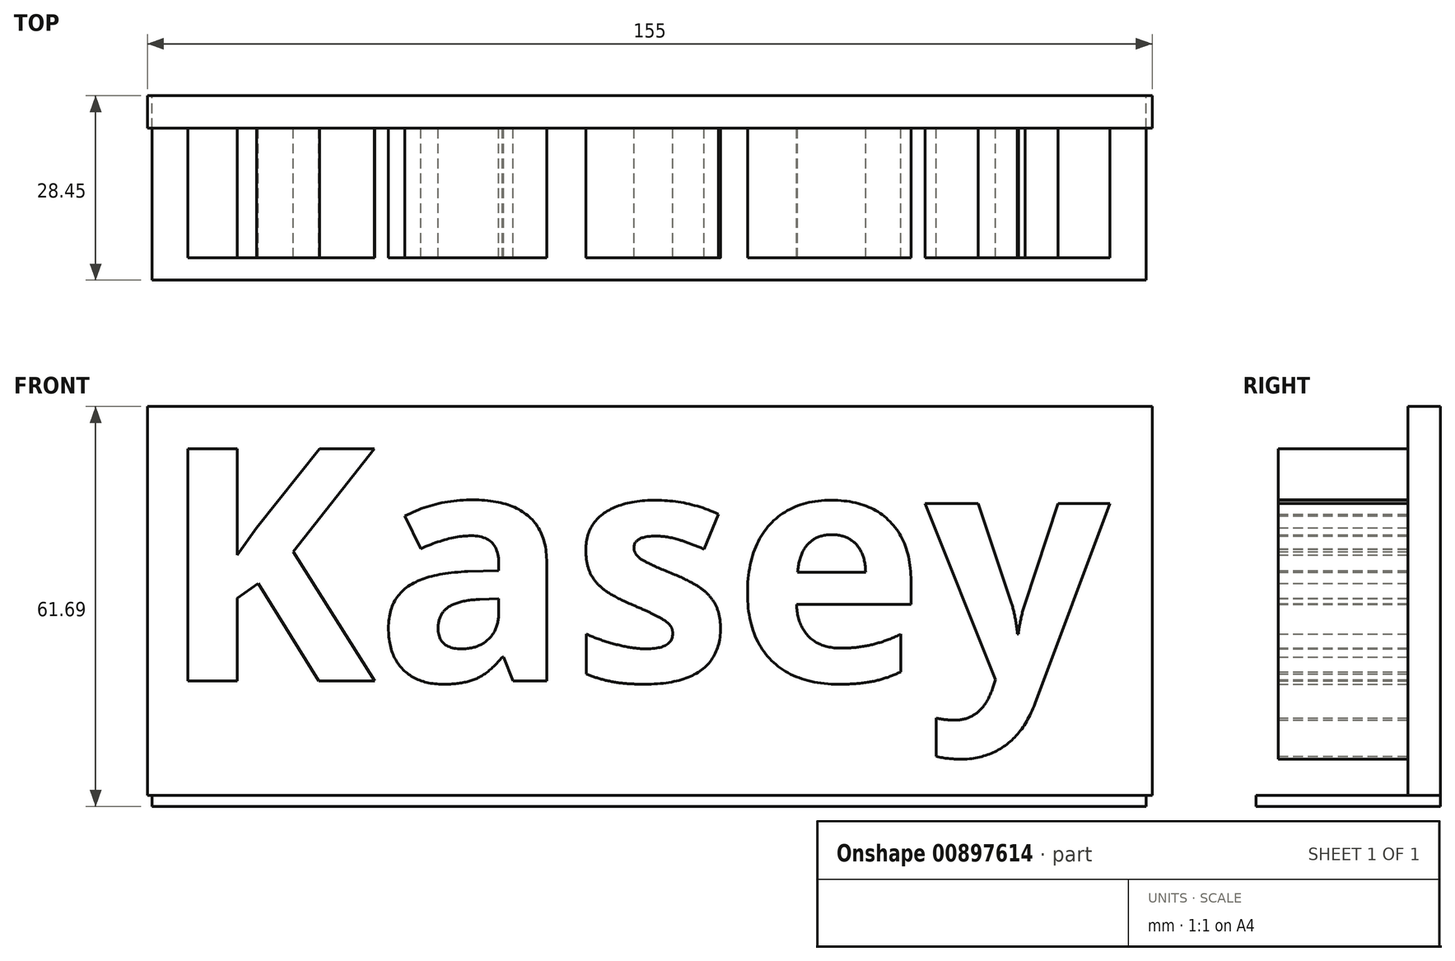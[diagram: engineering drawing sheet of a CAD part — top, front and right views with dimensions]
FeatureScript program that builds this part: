
annotation { "Feature Type Name" : "Feature", "Feature Type Description" : "" }
export const myFeature = defineFeature(function(context is Context, id is Id, definition is map)
    precondition{}
    {
        {
            var Q0;
            Q0=qCreatedBy(makeId("Front.planeOp"),FACE);
            var sketch = newSketch(context, id + "F0", { "sketchPlane" : qUnion([Q0])});
            skText(sketch, "E0", { "text": "Kasey", "fontName": "OpenSans-Bold.ttf"});
            const initialGuessF0  = {"E0": [-0.075, 0.01298, 1, 0, 0.03612]};
            skSetInitialGuess(sketch, initialGuessF0);
            skSolve(sketch);
        }
        {
            var Q0;
            Q0=qCreatedBy(makeId("Front.planeOp"),FACE);
            var sketch = newSketch(context, id + "F1", { "sketchPlane" : qUnion([Q0])});
            skLineSegment(sketch, "E1.bottom", {"start": v(-76.76, 55.33) * mm, "end": v(78.24, 55.33) * mm});
            skLineSegment(sketch, "E1.top", {"start": v(-76.76, -4.67) * mm, "end": v(78.24, -4.67) * mm});
            skLineSegment(sketch, "E1.left", {"start": v(-76.76, 55.33) * mm, "end": v(-76.76, -4.67) * mm});
            skLineSegment(sketch, "E1.right", {"start": v(78.24, 55.33) * mm, "end": v(78.24, -4.67) * mm});
            skSolve(sketch);
        }
        {
            var Q0;
            Q0=makeQuery(id+"F1.imprint","IMPRINT",FACE,{"disambiguationData":[TD([[makeQuery(id+"F1.imprint","IMPRINT",EDGE,{"derivedFrom":sQuery(id+"F1.wireOp",EDGE,"E1.bottom")}),-1.0]])]});
            extrude(context, id + "F2", {"entities" : qUnion([Q0]), "depth" : 5 * mm, "offsetDistance" : 25.4 * mm});
        }
        {
            var Q0;
            Q0 = qSketchRegion(id + "F0", true);
            extrude(context, id + "F3", {"entities" : qUnion([Q0]), "operationType" : NewBodyOperationType.ADD, "depth" : 25 * mm, "offsetDistance" : 25.4 * mm});
        }
        {
            var Q0;
            Q0=qCreatedBy(makeId("Front.planeOp"),FACE);
            var sketch = newSketch(context, id + "F4", { "sketchPlane" : qUnion([Q0])});
            skLineSegment(sketch, "E2.bottom", {"start": v(-76.06, -4.67) * mm, "end": v(77.33, -4.67) * mm});
            skLineSegment(sketch, "E2.top", {"start": v(-76.06, -6.36) * mm, "end": v(77.33, -6.36) * mm});
            skLineSegment(sketch, "E2.left", {"start": v(-76.06, -4.67) * mm, "end": v(-76.06, -6.36) * mm});
            skLineSegment(sketch, "E2.right", {"start": v(77.33, -4.67) * mm, "end": v(77.33, -6.36) * mm});
            skSolve(sketch);
        }
        {
            var Q0;
            Q0=makeQuery(id+"F4.imprint","IMPRINT",FACE,{"disambiguationData":[TD([[makeQuery(id+"F4.imprint","IMPRINT",EDGE,{"derivedFrom":sQuery(id+"F4.wireOp",EDGE,"E2.bottom")}),-1.0]])]});
            extrude(context, id + "F5", {"entities" : qUnion([Q0]), "operationType" : NewBodyOperationType.ADD, "depth" : 28.45 * mm, "offsetDistance" : 25.4 * mm});
        }
    });
